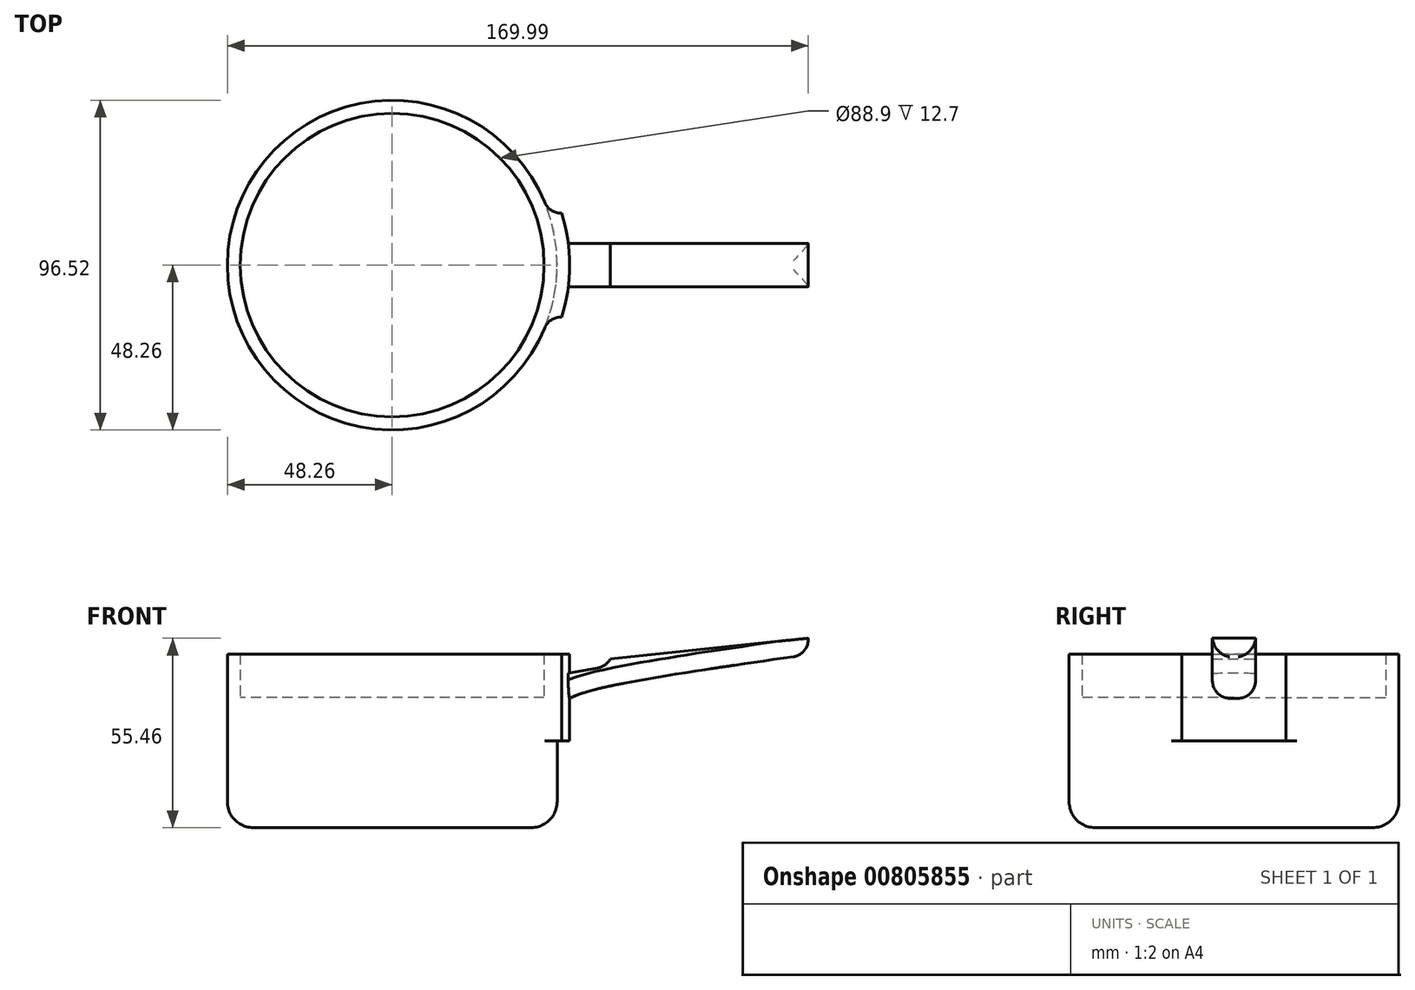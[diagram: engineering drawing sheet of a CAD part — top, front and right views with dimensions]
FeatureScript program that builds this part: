
annotation { "Feature Type Name" : "Feature", "Feature Type Description" : "" }
export const myFeature = defineFeature(function(context is Context, id is Id, definition is map)
    precondition{}
    {
        {
            var Q0;
            Q0=qCreatedBy(makeId("Right.planeOp"),FACE);
            var sketch = newSketch(context, id + "F0", { "sketchPlane" : qUnion([Q0])});
            skLineSegment(sketch, "E0", {"start": v(0, 0) * mm, "end": v(40.64, 0) * mm});
            skLineSegment(sketch, "E1", {"start": v(0, 0) * mm, "end": v(0, 3.81) * mm});
            skLineSegment(sketch, "E2", {"start": v(0, 3.81) * mm, "end": v(39.8, 3.81) * mm});
            skArc(sketch, "E3", {"start": v(39.8, 3.81) * mm, "mid": v(43.09, 5.17) * mm, "end": v(44.45, 8.45) * mm});
            skLineSegment(sketch, "E4", {"start": v(44.45, 25.4) * mm, "end": v(44.45, 8.45) * mm});
            skLineSegment(sketch, "E5", {"start": v(44.45, 25.4) * mm, "end": v(48.26, 25.4) * mm});
            skLineSegment(sketch, "E6", {"start": v(48.26, 25.4) * mm, "end": v(48.26, 7.62) * mm});
            skArc(sketch, "E7", {"start": v(40.64, 0) * mm, "mid": v(46.03, 2.23) * mm, "end": v(48.26, 7.62) * mm});
            skSolve(sketch);
        }
        {
            var Q0;
            Q0=makeQuery(id+"F0.imprint","IMPRINT",FACE,{"disambiguationData":[TD([[makeQuery(id+"F0.imprint","IMPRINT",EDGE,{"derivedFrom":sQuery(id+"F0.wireOp",EDGE,"E0")}),1.0]])]});
            var Q1;
            Q1=sQuery(id+"F0.wireOp",EDGE,"E1");
            revolve(context, id + "F1", {"surfaceOperationType" : NewSurfaceOperationType.NEW, "entities" : qUnion([Q0]), "axis" : qUnion([Q1]), "revolveType" : RevolveType.FULL});
        }
        {
            var Q0;
            Q0=makeQuery(id+"F1.opRevolve","SWEPT_FACE",FACE,{"disambiguationData":[OSD([sQuery(id+"F0.wireOp",EDGE,"E5")])]});
            var sketch = newSketch(context, id + "F2", { "sketchPlane" : qUnion([Q0])});
            skArc(sketch, "E8", {"start": v(49.6, -15.24) * mm, "mid": v(51.89, 0) * mm, "end": v(49.6, 15.24) * mm});
            skLineSegment(sketch, "E9", {"start": v(49.6, -15.24) * mm, "end": v(45.8, -15.24) * mm});
            skLineSegment(sketch, "E10", {"start": v(49.6, 15.24) * mm, "end": v(45.8, 15.24) * mm});
            skCircle(sketch, "E11", {"center": v(0, 0) * mm, "radius": 48.26 * mm});
            skSolve(sketch);
        }
        {
            var Q0;
            Q0=makeQuery(id+"F2.imprint","IMPRINT",FACE,{"disambiguationData":[TD([[makeQuery(id+"F2.imprint","IMPRINT",EDGE,{"derivedFrom":makeQuery(id+"F1.opRevolve","SWEPT_EDGE",EDGE,{"disambiguationData":[OSD([sQuery(id+"F0.wireOp",EDGE,"E4"),sQuery(id+"F0.wireOp",EDGE,"E5")])]})}),1.0]])]});
            var Q1;
            Q1=makeQuery(id+"F2.imprint","IMPRINT",FACE,{"disambiguationData":[TD([[makeQuery(id+"F2.imprint","IMPRINT",EDGE,{"derivedFrom":sQuery(id+"F2.wireOp",EDGE,"E8")}),1.0]])]});
            extrude(context, id + "F3", {"entities" : qUnion([Q0, Q1]), "operationType" : NewBodyOperationType.ADD, "depth" : 25.4 * mm, "offsetDistance" : 25.4 * mm});
        }
        {
            var Q0;
            Q0=makeQuery(id+"F3.opExtrude","SWEPT_EDGE",EDGE,{"disambiguationData":[OSD([sQuery(id+"F2.wireOp",EDGE,"E9"),sQuery(id+"F2.wireOp",EDGE,"E11")])]});
            var Q1;
            Q1=makeQuery(id+"F1.opRevolve","SWEPT_EDGE",EDGE,{"disambiguationData":[OSD([sQuery(id+"F0.wireOp",EDGE,"E5"),sQuery(id+"F0.wireOp",EDGE,"E6")])]});
            var Q2;
            Q2=makeQuery(id+"F3.opExtrude","SWEPT_EDGE",EDGE,{"disambiguationData":[OSD([sQuery(id+"F2.wireOp",EDGE,"E10"),sQuery(id+"F2.wireOp",EDGE,"E11")])]});
            fillet(context, id + "F4", {"entities" : qUnion([Q0, Q1, Q2]), "radius" : 5.08 * mm, "tangentPropagation" : true, "allowEdgeOverflow" : false});
        }
        {
            var Q0;
            Q0=qCreatedBy(makeId("Front.planeOp"),FACE);
            var sketch = newSketch(context, id + "F5", { "sketchPlane" : qUnion([Q0])});
            skFitSpline(sketch, "E12", {"points": [v(49.31, 36.31) * mm, v(55.63, 39.4) * mm, v(121.9, 50.69) * mm], "startDerivative": vector(18.3, 12.36) * mm, "endDerivative": vector(111.06, 15.8) * mm});
            skLineSegment(sketch, "E13", {"start": v(121.72, 55.46) * mm, "end": v(121.9, 50.69) * mm});
            skLineSegment(sketch, "E14", {"start": v(49.7, 44.93) * mm, "end": v(64.16, 47.46) * mm});
            skLineSegment(sketch, "E15", {"start": v(64.16, 47.46) * mm, "end": v(63.81, 49.45) * mm});
            skLineSegment(sketch, "E16", {"start": v(63.81, 49.45) * mm, "end": v(121.72, 55.46) * mm});
            skLineSegment(sketch, "E17", {"start": v(49.7, 44.93) * mm, "end": v(49.31, 36.31) * mm});
            skSolve(sketch);
        }
        {
            var Q0;
            Q0 = qSketchRegion(id + "F5", true);
            extrude(context, id + "F6", {"entities" : qUnion([Q0]), "operationType" : NewBodyOperationType.ADD, "endBound" : BoundingType.SYMMETRIC, "depth" : 12.7 * mm, "offsetDistance" : 25.4 * mm});
        }
        {
            var Q0;
            Q0=makeQuery(id+"F6.opExtrude","CAP_EDGE",EDGE,{"disambiguationData":[OSD([sQuery(id+"F5.wireOp",EDGE,"E12")])],"isStart":false});
            var Q1;
            Q1=makeQuery(id+"F6.opExtrude","CAP_EDGE",EDGE,{"disambiguationData":[OSD([sQuery(id+"F5.wireOp",EDGE,"E12")])],"isStart":true});
            var Q2;
            Q2=makeQuery(id+"F6.opExtrude","SWEPT_EDGE",EDGE,{"disambiguationData":[OSD([sQuery(id+"F5.wireOp",EDGE,"E12"),sQuery(id+"F5.wireOp",EDGE,"E13")])]});
            fillet(context, id + "F7", {"entities" : qUnion([Q0, Q1, Q2]), "radius" : 5.08 * mm, "tangentPropagation" : true, "allowEdgeOverflow" : false});
        }
        {
            var Q0;
            Q0=makeQuery(id+"F6.opExtrude","SWEPT_EDGE",EDGE,{"disambiguationData":[OSD([sQuery(id+"F5.wireOp",EDGE,"E14"),sQuery(id+"F5.wireOp",EDGE,"E15")])]});
            fillet(context, id + "F8", {"entities" : qUnion([Q0]), "radius" : 5.08 * mm, "tangentPropagation" : true, "allowEdgeOverflow" : false});
        }
        {
            var Q0;
            Q0=qCreatedBy(makeId("Top.planeOp"),FACE);
            cPlane(context, id + "F9", {"entities" : qUnion([Q0]), "cplaneType" : CPlaneType.OFFSET, "offset" : 38.1 * mm, "width" : 152.4 * mm, "height" : 152.4 * mm});
        }
        {
            var Q0;
            Q0=qCreatedBy(id+"F9.planeOp",FACE);
            var sketch = newSketch(context, id + "F10", { "sketchPlane" : qUnion([Q0])});
            skCircle(sketch, "E18", {"center": v(0, 0) * mm, "radius": 46.43 * mm});
            skSolve(sketch);
        }
        {
            var Q0;
            Q0 = qSketchRegion(id + "F10", true);
            extrude(context, id + "F11", {"entities" : qUnion([Q0]), "operationType" : NewBodyOperationType.ADD, "endBound" : BoundingType.UP_TO_NEXT, "oppositeDirection" : true, "depth" : 25.4 * mm, "offsetDistance" : 25.4 * mm});
        }
    });
